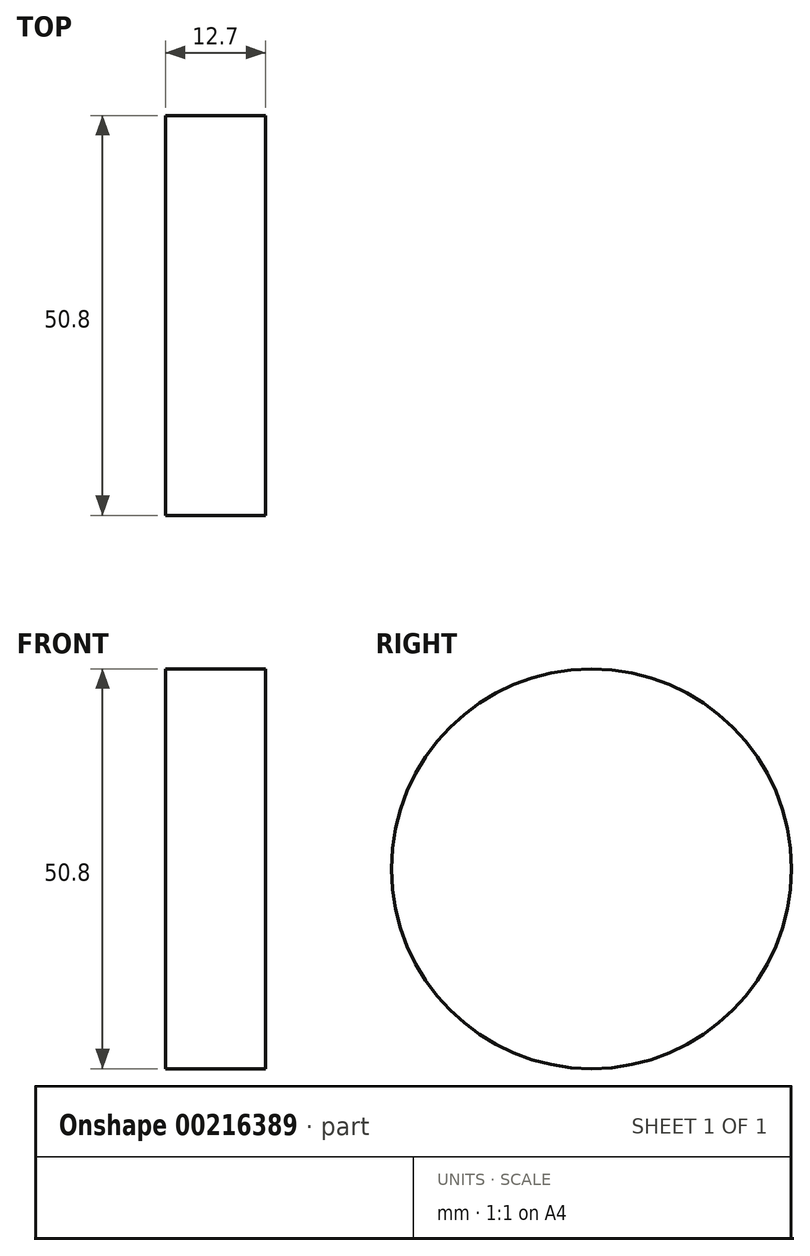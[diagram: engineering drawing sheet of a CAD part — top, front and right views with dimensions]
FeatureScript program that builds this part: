
annotation { "Feature Type Name" : "Feature", "Feature Type Description" : "" }
export const myFeature = defineFeature(function(context is Context, id is Id, definition is map)
    precondition{}
    {
        {
            var Q0;
            Q0=qCreatedBy(makeId("Right.planeOp"),FACE);
            var sketch = newSketch(context, id + "F0", { "sketchPlane" : qUnion([Q0])});
            skCircle(sketch, "E0", {"center": v(0, 0) * mm, "radius": 25.4 * mm});
            skSolve(sketch);
        }
        {
            var Q0;
            Q0=qSketchRegion(id+"F0",true);
            extrude(context, id + "F1", {"entities" : qUnion([Q0]), "depth" : 12.7 * mm});
        }
    });
